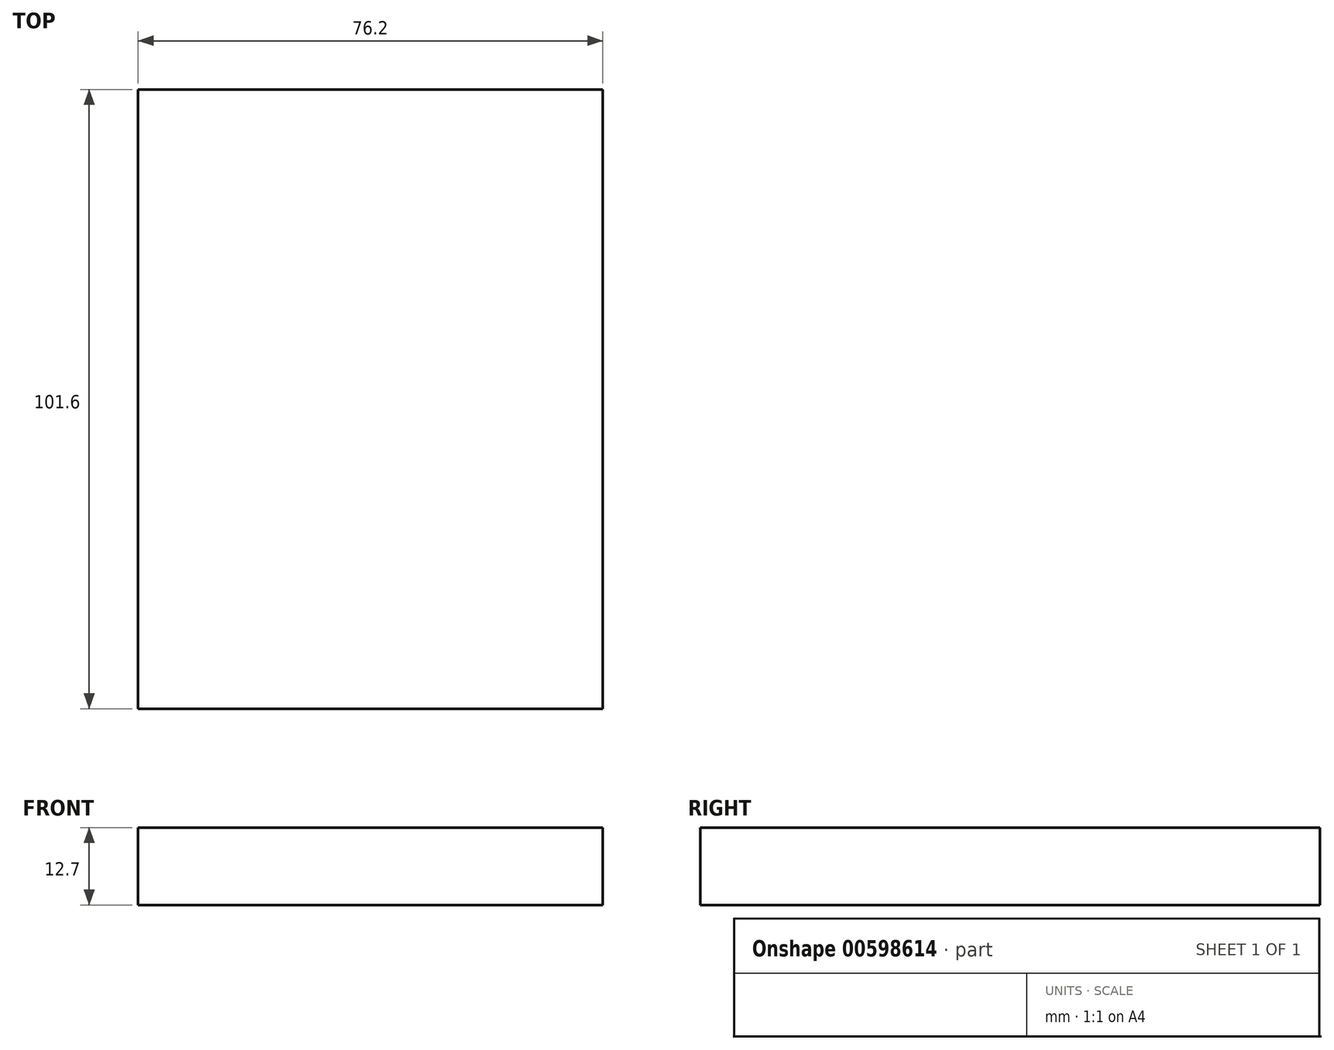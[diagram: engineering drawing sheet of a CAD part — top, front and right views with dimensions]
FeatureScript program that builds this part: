
annotation { "Feature Type Name" : "Feature", "Feature Type Description" : "" }
export const myFeature = defineFeature(function(context is Context, id is Id, definition is map)
    precondition{}
    {
        {
            var Q0;
            Q0=qCreatedBy(makeId("Top.planeOp"),FACE);
            var sketch = newSketch(context, id + "F0", { "sketchPlane" : qUnion([Q0])});
            skLineSegment(sketch, "E0.bottom", {"start": v(-67.36, 46.65) * mm, "end": v(8.84, 46.65) * mm});
            skLineSegment(sketch, "E0.top", {"start": v(-67.36, -54.95) * mm, "end": v(8.84, -54.95) * mm});
            skLineSegment(sketch, "E0.left", {"start": v(-67.36, 46.65) * mm, "end": v(-67.36, -54.95) * mm});
            skLineSegment(sketch, "E0.right", {"start": v(8.84, 46.65) * mm, "end": v(8.84, -54.95) * mm});
            skSolve(sketch);
        }
        {
            var Q0;
            Q0=makeQuery(id+"F0.imprint","IMPRINT",FACE,{"disambiguationData":[TD([[makeQuery(id+"F0.imprint","IMPRINT",EDGE,{"derivedFrom":sQuery(id+"F0.wireOp",EDGE,"E0.bottom")}),-1.0]])]});
            extrude(context, id + "F1", {"entities" : qUnion([Q0]), "depth" : 12.7 * mm, "offsetDistance" : 25.4 * mm});
        }
    });
